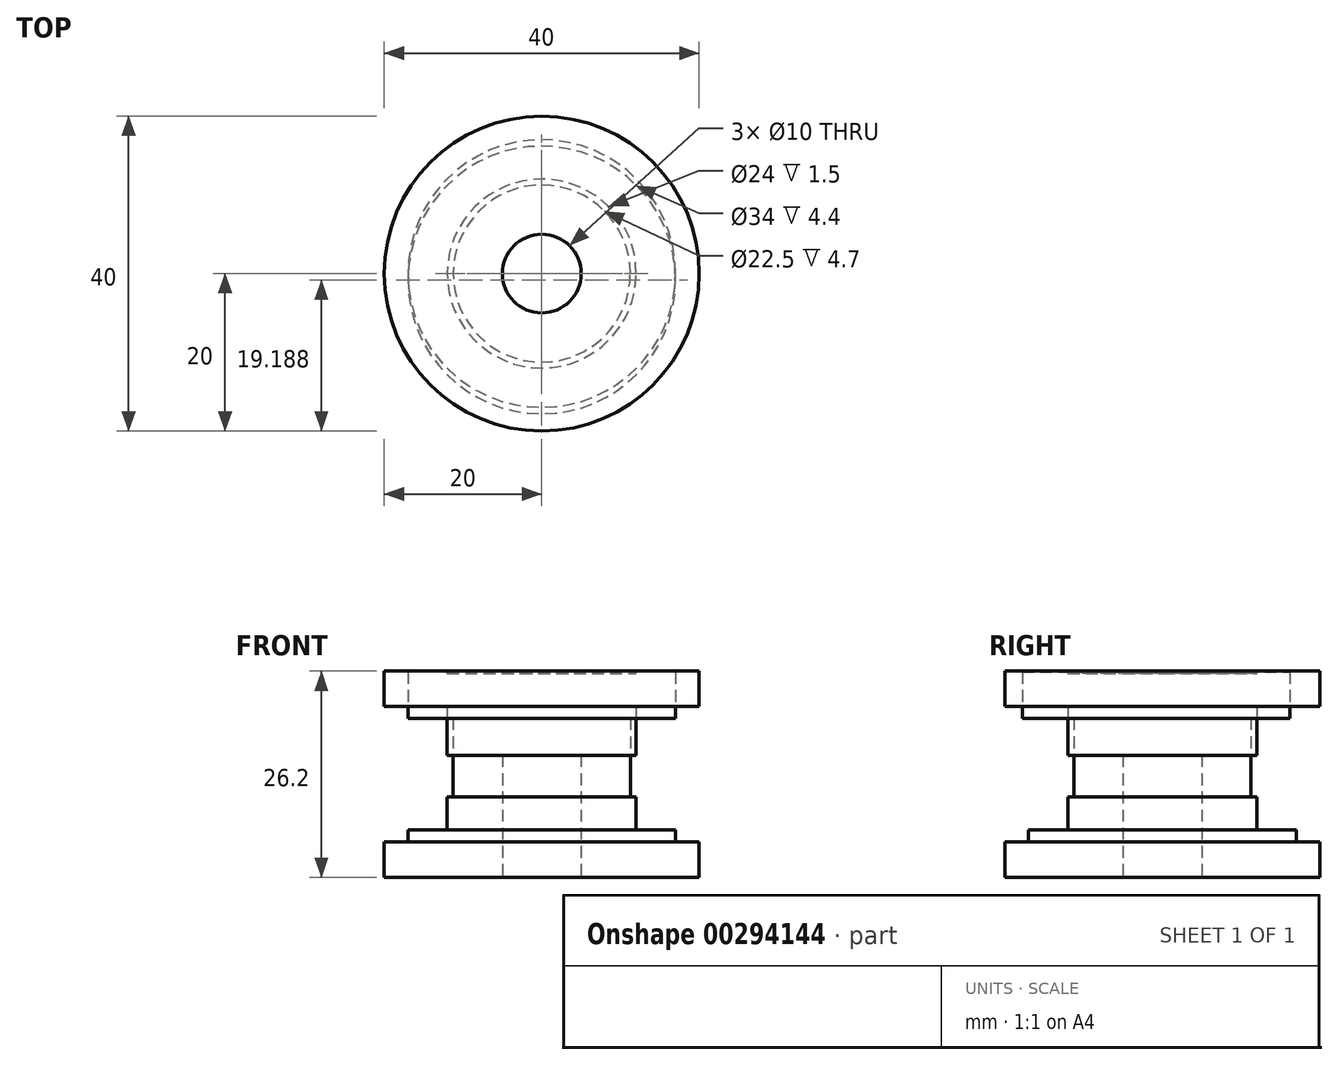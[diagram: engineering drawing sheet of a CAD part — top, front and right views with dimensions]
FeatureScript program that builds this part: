
annotation { "Feature Type Name" : "Feature", "Feature Type Description" : "" }
export const myFeature = defineFeature(function(context is Context, id is Id, definition is map)
    precondition{}
    {
        {
            var Q0;
            Q0=qCreatedBy(makeId("Top.planeOp"),FACE);
            var sketch = newSketch(context, id + "F0", { "sketchPlane" : qUnion([Q0])});
            skCircle(sketch, "E0", {"center": v(0, 0) * mm, "radius": 20 * mm});
            skCircle(sketch, "E1", {"center": v(0, 0) * mm, "radius": 17 * mm});
            skCircle(sketch, "E2", {"center": v(0, 0) * mm, "radius": 11.25 * mm});
            skCircle(sketch, "E3", {"center": v(0, 0) * mm, "radius": 12 * mm});
            skCircle(sketch, "E4", {"center": v(0, 0) * mm, "radius": 5 * mm});
            skSolve(sketch);
        }
        {
            var Q0;
            Q0=makeQuery(id+"F0.imprint","IMPRINT",FACE,{"disambiguationData":[TD([[makeQuery(id+"F0.imprint","IMPRINT",EDGE,{"derivedFrom":sQuery(id+"F0.wireOp",EDGE,"E0")}),1.0]])]});
            extrude(context, id + "F1", {"entities" : qUnion([Q0]), "depth" : 4.5 * mm});
        }
        {
            var Q0;
            Q0=makeQuery(id+"F0.imprint","IMPRINT",FACE,{"disambiguationData":[TD([[makeQuery(id+"F0.imprint","IMPRINT",EDGE,{"derivedFrom":sQuery(id+"F0.wireOp",EDGE,"E1")}),1.0]])]});
            extrude(context, id + "F2", {"entities" : qUnion([Q0]), "operationType" : NewBodyOperationType.ADD, "depth" : 6 * mm});
        }
        {
            var Q0;
            Q0=makeQuery(id+"F0.imprint","IMPRINT",FACE,{"disambiguationData":[TD([[makeQuery(id+"F0.imprint","IMPRINT",EDGE,{"derivedFrom":sQuery(id+"F0.wireOp",EDGE,"E2")}),-1.0]])]});
            extrude(context, id + "F3", {"entities" : qUnion([Q0]), "operationType" : NewBodyOperationType.ADD, "depth" : 10.25 * mm});
        }
        {
            var Q0;
            Q0=makeQuery(id+"F0.imprint","IMPRINT",FACE,{"disambiguationData":[TD([[makeQuery(id+"F0.imprint","IMPRINT",EDGE,{"derivedFrom":sQuery(id+"F0.wireOp",EDGE,"E2")}),1.0]])]});
            extrude(context, id + "F4", {"entities" : qUnion([Q0]), "operationType" : NewBodyOperationType.ADD, "depth" : 15.5 * mm});
        }
        {
            var Q0;
            Q0=makeQuery(id+"F4.opExtrude","CAP_FACE",FACE,{"disambiguationData":[OSD([sQuery(id+"F0.wireOp",EDGE,"E2"),sQuery(id+"F0.wireOp",EDGE,"E4")])],"isStart":false});
            var sketch = newSketch(context, id + "F5", { "sketchPlane" : qUnion([Q0])});
            skCircle(sketch, "E5", {"center": v(0, 0) * mm, "radius": 12 * mm});
            skCircle(sketch, "E6", {"center": v(0, 0) * mm, "radius": 17 * mm});
            skCircle(sketch, "E7", {"center": v(0, 0) * mm, "radius": 20 * mm});
            skSolve(sketch);
        }
        {
            var Q0;
            Q0=makeQuery(id+"F5.imprint","IMPRINT",FACE,{"disambiguationData":[TD([[makeQuery(id+"F5.imprint","IMPRINT",EDGE,{"derivedFrom":sQuery(id+"F5.wireOp",EDGE,"E5")}),1.0]])]});
            extrude(context, id + "F6", {"entities" : qUnion([Q0]), "operationType" : NewBodyOperationType.ADD, "depth" : 4.7 * mm});
        }
        {
            var Q0;
            Q0=makeQuery(id+"F6.opExtrude","CAP_FACE",FACE,{"disambiguationData":[OSD([sQuery(id+"F0.wireOp",EDGE,"E2"),sQuery(id+"F5.wireOp",EDGE,"E5")])],"isStart":false});
            var sketch = newSketch(context, id + "F7", { "sketchPlane" : qUnion([Q0])});
            skCircle(sketch, "E8", {"center": v(0, -0.81) * mm, "radius": 17 * mm});
            skSolve(sketch);
        }
        {
            var Q0;
            Q0=makeQuery(id+"F7.imprint","IMPRINT",FACE,{"disambiguationData":[TD([[makeQuery(id+"F7.imprint","IMPRINT",EDGE,{"derivedFrom":sQuery(id+"F7.wireOp",EDGE,"E8")}),1.0]])]});
            extrude(context, id + "F8", {"entities" : qUnion([Q0]), "depth" : 1.5 * mm});
        }
        {
            var Q0;
            Q0=makeQuery(id+"F8.opExtrude","CAP_FACE",FACE,{"disambiguationData":[OSD([sQuery(id+"F5.wireOp",EDGE,"E5"),sQuery(id+"F7.wireOp",EDGE,"E8")])],"isStart":false});
            var sketch = newSketch(context, id + "F9", { "sketchPlane" : qUnion([Q0])});
            skCircle(sketch, "E9", {"center": v(0, 0) * mm, "radius": 20 * mm});
            skSolve(sketch);
        }
        {
            var Q0;
            Q0=makeQuery(id+"F9.imprint","IMPRINT",FACE,{"disambiguationData":[TD([[makeQuery(id+"F9.imprint","IMPRINT",EDGE,{"derivedFrom":sQuery(id+"F9.wireOp",EDGE,"E9")}),1.0]])]});
            extrude(context, id + "F10", {"entities" : qUnion([Q0]), "depth" : 4.5 * mm});
        }
        {
            var Q0;
            Q0=makeQuery(id+"F10.opExtrude","CAP_FACE",FACE,{"disambiguationData":[OSD([sQuery(id+"F7.wireOp",EDGE,"E8"),sQuery(id+"F9.wireOp",EDGE,"E9")])],"isStart":false});
            var sketch = newSketch(context, id + "F11", { "sketchPlane" : qUnion([Q0])});
            skCircle(sketch, "E10", {"center": v(0, 0) * mm, "radius": 20 * mm});
            skSolve(sketch);
        }
        {
            var Q0;
            Q0 = qSketchRegion(id + "F11", true);
            extrude(context, id + "F12", {"entities" : qUnion([Q0]), "operationType" : NewBodyOperationType.ADD, "oppositeDirection" : true, "depth" : 0.1 * mm});
        }
        {
            var Q0;
            Q0=makeQuery(id+"F12.opExtrude","CAP_FACE",FACE,{"disambiguationData":[OSD([sQuery(id+"F11.wireOp",EDGE,"E10")])],"isStart":false});
            var sketch = newSketch(context, id + "F13", { "sketchPlane" : qUnion([Q0])});
            skCircle(sketch, "E11", {"center": v(0, 0) * mm, "radius": 5 * mm});
            skSolve(sketch);
        }
        {
            var Q0;
            Q0=makeQuery(id+"F13.imprint","IMPRINT",FACE,{"disambiguationData":[TD([[makeQuery(id+"F13.imprint","IMPRINT",EDGE,{"derivedFrom":sQuery(id+"F13.wireOp",EDGE,"E11")}),1.0]])]});
            extrude(context, id + "F14", {"entities" : qUnion([Q0]), "operationType" : NewBodyOperationType.REMOVE, "oppositeDirection" : true, "depth" : 79 * mm});
        }
        {
            var Q0;
            Q0=makeQuery(id+"F12.opExtrude","CAP_FACE",FACE,{"disambiguationData":[OSD([sQuery(id+"F11.wireOp",EDGE,"E10")])],"isStart":false});
            var sketch = newSketch(context, id + "F15", { "sketchPlane" : qUnion([Q0])});
            skCircle(sketch, "E12", {"center": v(0, 0) * mm, "radius": 12 * mm});
            skSolve(sketch);
        }
        {
            var Q0;
            Q0=makeQuery(id+"F15.imprint","IMPRINT",FACE,{"disambiguationData":[TD([[makeQuery(id+"F15.imprint","IMPRINT",EDGE,{"derivedFrom":sQuery(id+"F15.wireOp",EDGE,"E12")}),1.0]])]});
            extrude(context, id + "F16", {"entities" : qUnion([Q0]), "depth" : 0.2 * mm});
        }
    });
